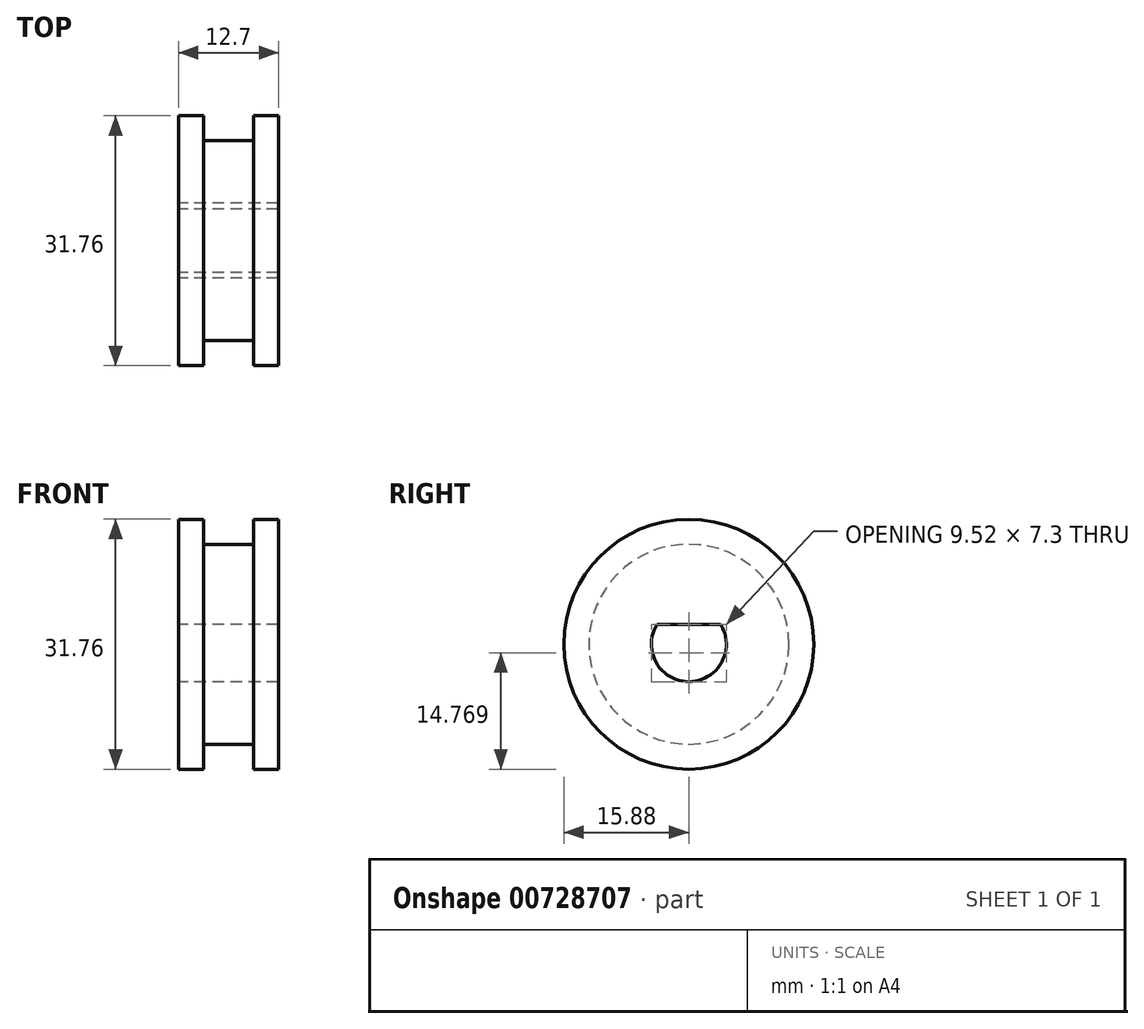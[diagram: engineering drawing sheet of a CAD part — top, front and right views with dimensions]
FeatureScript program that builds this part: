
annotation { "Feature Type Name" : "Feature", "Feature Type Description" : "" }
export const myFeature = defineFeature(function(context is Context, id is Id, definition is map)
    precondition{}
    {
        {
            var Q0;
            Q0=qCreatedBy(makeId("Front.planeOp"),FACE);
            var sketch = newSketch(context, id + "F0", { "sketchPlane" : qUnion([Q0])});
            skLineSegment(sketch, "E0", {"start": v(-15.1, 0) * mm, "end": v(15.1, 0) * mm, "construction": true});
            skLineSegment(sketch, "E1", {"start": v(-6.35, 4.76) * mm, "end": v(-6.35, 15.88) * mm});
            skLineSegment(sketch, "E2", {"start": v(-6.35, 15.88) * mm, "end": v(-3.17, 15.88) * mm});
            skLineSegment(sketch, "E3", {"start": v(-3.17, 15.88) * mm, "end": v(-3.17, 12.7) * mm});
            skLineSegment(sketch, "E4", {"start": v(-3.17, 12.7) * mm, "end": v(3.17, 12.7) * mm});
            skLineSegment(sketch, "E5", {"start": v(3.17, 12.7) * mm, "end": v(3.17, 15.88) * mm});
            skLineSegment(sketch, "E6", {"start": v(3.17, 15.88) * mm, "end": v(6.35, 15.88) * mm});
            skLineSegment(sketch, "E7", {"start": v(6.35, 15.88) * mm, "end": v(6.35, 4.76) * mm});
            skLineSegment(sketch, "E8", {"start": v(6.35, 4.76) * mm, "end": v(-6.35, 4.76) * mm});
            skPoint(sketch, "E9", {"position": v(0, 12.7) * mm});
            skSolve(sketch);
        }
        {
            var Q0;
            Q0 = qSketchRegion(id + "F0", true);
            var Q1;
            Q1=sQuery(id+"F0.wireOp",EDGE,"E0");
            revolve(context, id + "F1", {"surfaceOperationType" : NewSurfaceOperationType.NEW, "entities" : qUnion([Q0]), "axis" : qUnion([Q1]), "revolveType" : RevolveType.FULL});
        }
        {
            var Q0;
            Q0=qCreatedBy(makeId("Right.planeOp"),FACE);
            var sketch = newSketch(context, id + "F2", { "sketchPlane" : qUnion([Q0])});
            skArc(sketch, "E10.0", {"start": v(4.03, 2.54) * mm, "mid": v(0, 4.76) * mm, "end": v(-4.03, 2.54) * mm});
            skLineSegment(sketch, "E11", {"start": v(-4.03, 2.54) * mm, "end": v(4.03, 2.54) * mm});
            skSolve(sketch);
        }
        {
            var Q0;
            Q0 = qSketchRegion(id + "F2", true);
            var Q1;
            Q1=makeQuery(id+"F1.opRevolve","SWEPT_FACE",FACE,{"disambiguationData":[OSD([sQuery(id+"F0.wireOp",EDGE,"E7")])]});
            var Q2;
            Q2=makeQuery(id+"F1.opRevolve","SWEPT_FACE",FACE,{"disambiguationData":[OSD([sQuery(id+"F0.wireOp",EDGE,"E1")])]});
            extrude(context, id + "F3", {"entities" : qUnion([Q0]), "operationType" : NewBodyOperationType.ADD, "endBound" : BoundingType.UP_TO_SURFACE, "depth" : 25.4 * mm, "endBoundEntityFace" : qUnion([Q1]), "offsetDistance" : 25.4 * mm, "hasSecondDirection" : true, "secondDirectionBound" : BoundingType.UP_TO_SURFACE, "secondDirectionOppositeDirection" : true, "secondDirectionDepth" : 25.4 * mm, "secondDirectionBoundEntityFace" : qUnion([Q2])});
        }
    });
